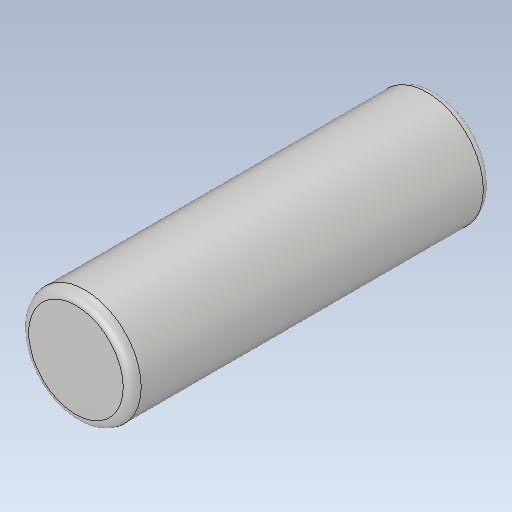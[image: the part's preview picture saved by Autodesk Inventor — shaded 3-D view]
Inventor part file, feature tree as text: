
AUTODESK INVENTOR PART (.ipt)
format: ipt  version: 2020.2 (Build 242310000, 310)  size: 116,224 bytes
history: native  units: mm
features: other x1, extrude x1, fillet x1, sketch x1
ambient origin geometry x8: Origin, YZ Plane, XZ Plane, XY Plane, X Axis, Y Axis, Z Axis, Center Point
bodies: Body1 (feature_tree)
feature tree (4):
  other  "ソリッド1"
  extrude  "押し出し1"  Depth=2.5mm
  fillet  "フィレット1"  Radius=8.0mm
  sketch  "スケッチ1"
